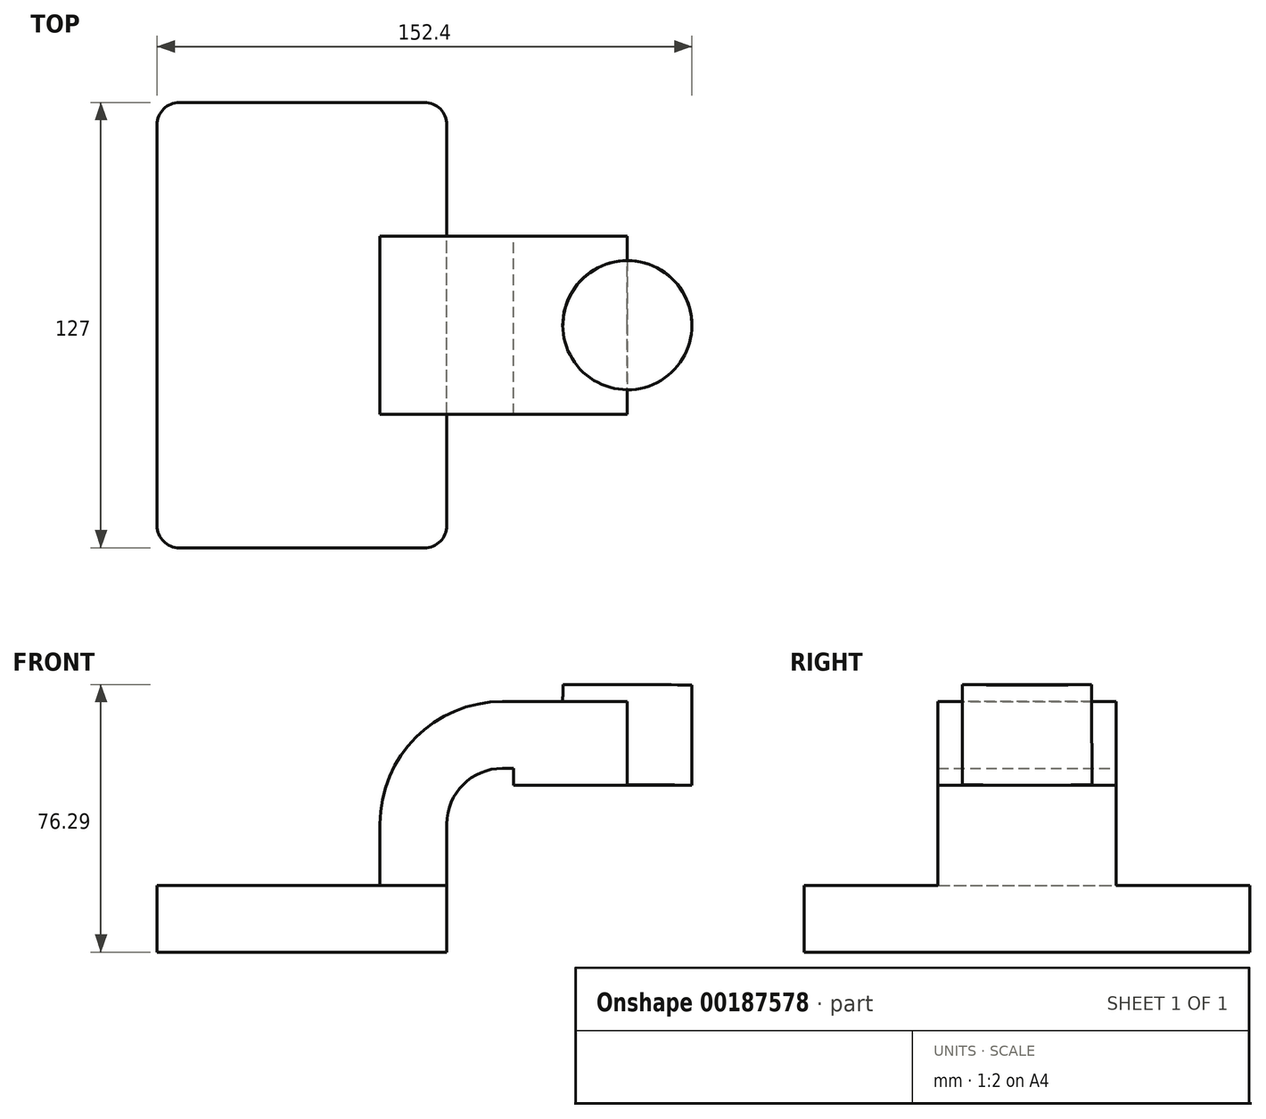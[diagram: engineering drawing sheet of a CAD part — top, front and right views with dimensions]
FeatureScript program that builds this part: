
annotation { "Feature Type Name" : "Feature", "Feature Type Description" : "" }
export const myFeature = defineFeature(function(context is Context, id is Id, definition is map)
    precondition{}
    {
        {
            var Q0;
            Q0=qCreatedBy(makeId("Front.planeOp"),FACE);
            var sketch = newSketch(context, id + "F0", { "sketchPlane" : qUnion([Q0])});
            skLineSegment(sketch, "E0.bottom", {"start": v(41.28, -9.52) * mm, "end": v(-41.28, -9.53) * mm});
            skLineSegment(sketch, "E0.top", {"start": v(41.28, 9.53) * mm, "end": v(-41.28, 9.53) * mm});
            skLineSegment(sketch, "E0.left", {"start": v(41.28, -9.52) * mm, "end": v(41.28, 9.53) * mm});
            skLineSegment(sketch, "E0.right", {"start": v(-41.28, -9.52) * mm, "end": v(-41.28, 9.53) * mm});
            skPoint(sketch, "E0.middle", {"position": v(0, 0) * mm});
            skLineSegment(sketch, "E1.bottom", {"start": v(111.12, 38.1) * mm, "end": v(60.32, 38.1) * mm});
            skLineSegment(sketch, "E1.top", {"start": v(111.12, 66.68) * mm, "end": v(60.32, 66.68) * mm});
            skLineSegment(sketch, "E1.left", {"start": v(111.12, 38.1) * mm, "end": v(111.12, 66.68) * mm});
            skLineSegment(sketch, "E1.right", {"start": v(60.32, 38.1) * mm, "end": v(60.32, 66.68) * mm});
            skPoint(sketch, "E1.middle", {"position": v(85.72, 52.39) * mm});
            skLineSegment(sketch, "E2", {"start": v(41.28, 9.53) * mm, "end": v(41.28, 27) * mm});
            skArc(sketch, "E3", {"start": v(41.27, 27) * mm, "mid": v(45.92, 38.23) * mm, "end": v(57.15, 42.88) * mm});
            skLineSegment(sketch, "E4", {"start": v(57.15, 42.88) * mm, "end": v(92.67, 42.88) * mm});
            skLineSegment(sketch, "E5.0", {"start": v(57.15, 61.93) * mm, "end": v(92.74, 61.93) * mm});
            skArc(sketch, "E5.1", {"start": v(22.23, 27) * mm, "mid": v(32.45, 51.7) * mm, "end": v(57.15, 61.93) * mm});
            skLineSegment(sketch, "E5.2", {"start": v(22.22, 9.53) * mm, "end": v(22.22, 27) * mm});
            skLineSegment(sketch, "E6", {"start": v(92.67, 38.1) * mm, "end": v(92.74, 66.68) * mm});
            skFitSpline(sketch, "E7", {"points": [v(-41.28, 9.53) * mm, v(60.32, 66.68) * mm], "startDerivative": vector(86.8, 95.5) * mm, "endDerivative": vector(118.36, 18.62) * mm});
            skSolve(sketch);
        }
        {
            var Q0;
            Q0=makeQuery(id+"F0.imprint","IMPRINT",FACE,{"disambiguationData":[TD([[makeQuery(id+"F0.imprint","IMPRINT",EDGE,{"derivedFrom":sQuery(id+"F0.wireOp",EDGE,"E0.bottom")}),-1.0]])]});
            extrude(context, id + "F1", {"entities" : qUnion([Q0]), "endBound" : BoundingType.SYMMETRIC, "depth" : 127 * mm});
        }
        {
            var Q0;
            {var subQ2=sQuery(id+"F0.wireOp",EDGE,"E2");Q0=makeQuery(id+"F0.imprint","IMPRINT",FACE,{"disambiguationData":[TD([[makeQuery(id+"F0.imprint","IMPRINT",EDGE,{"derivedFrom":subQ2}),1.0]])]});}
            extrude(context, id + "F2", {"entities" : qUnion([Q0]), "operationType" : NewBodyOperationType.ADD, "endBound" : BoundingType.SYMMETRIC, "depth" : 50.8 * mm});
        }
        {
            var Q0;
            {var subQ4=sQuery(id+"F0.wireOp",EDGE,"E5.1");Q0=makeQuery(id+"F0.imprint","IMPRINT",FACE,{"disambiguationData":[TD([[makeQuery(id+"F0.imprint","IMPRINT",EDGE,{"derivedFrom":subQ4}),1.0]])]});}
            extrude(context, id + "F3", {"entities" : qUnion([Q0]), "operationType" : NewBodyOperationType.ADD, "endBound" : BoundingType.SYMMETRIC, "depth" : 15.88 * mm});
        }
        {
            var Q0;
            {var subQ0=sQuery(id+"F0.wireOp",EDGE,"E1.right");var subQ1=sQuery(id+"F0.wireOp",EDGE,"E1.bottom");var subQ2=makeQuery(id+"F0.imprint","INTERSECT",VERTEX,{"derivedFrom":[subQ1,subQ0]});Q0=makeQuery(id+"F0.imprint","IMPRINT",FACE,{"disambiguationData":[TD([[makeQuery(id+"F0.imprint","IMPRINT",EDGE,{"disambiguationData":[TD([[subQ2,1.0]])],"derivedFrom":subQ1}),-1.0]])]});}
            extrude(context, id + "F4", {"entities" : qUnion([Q0]), "operationType" : NewBodyOperationType.ADD, "endBound" : BoundingType.SYMMETRIC, "depth" : 50.8 * mm});
        }
        {
            var Q0;
            Q0=makeQuery(id+"F1.opExtrude","CAP_EDGE",EDGE,{"disambiguationData":[OSD([sQuery(id+"F0.wireOp",EDGE,"E0.right")])],"isStart":false});
            var Q1;
            Q1=makeQuery(id+"F1.opExtrude","CAP_EDGE",EDGE,{"disambiguationData":[OSD([sQuery(id+"F0.wireOp",EDGE,"E0.left")])],"isStart":false});
            var Q2;
            Q2=makeQuery(id+"F1.opExtrude","CAP_EDGE",EDGE,{"disambiguationData":[OSD([sQuery(id+"F0.wireOp",EDGE,"E0.left")])],"isStart":true});
            var Q3;
            Q3=makeQuery(id+"F1.opExtrude","CAP_EDGE",EDGE,{"disambiguationData":[OSD([sQuery(id+"F0.wireOp",EDGE,"E0.right")])],"isStart":true});
            fillet(context, id + "F5", {"entities" : qUnion([Q0, Q1, Q2, Q3]), "radius" : 6.35 * mm, "tangentPropagation" : true, "allowEdgeOverflow" : false});
        }
        {
            var Q0;
            {var subQ4=sQuery(id+"F0.wireOp",EDGE,"E1.left");Q0=makeQuery(id+"F0.imprint","IMPRINT",FACE,{"disambiguationData":[TD([[makeQuery(id+"F0.imprint","IMPRINT",EDGE,{"derivedFrom":subQ4}),1.0]])]});}
            var Q1;
            Q1=sQuery(id+"F0.wireOp",EDGE,"E6");
            revolve(context, id + "F6", {"operationType" : NewBodyOperationType.ADD, "entities" : qUnion([Q0]), "axis" : qUnion([Q1]), "revolveType" : RevolveType.FULL});
        }
    });
